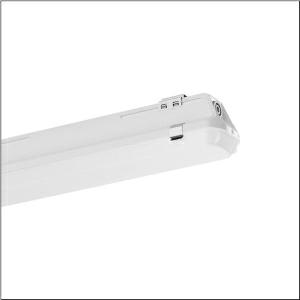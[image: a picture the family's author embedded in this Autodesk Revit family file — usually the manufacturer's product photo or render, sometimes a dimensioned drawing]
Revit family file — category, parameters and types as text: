
# Revit family: monsun_r__11_51fp10ep430h_21f7
name_source: partatom
category: Lighting Fixtures
units: mm (PartAtom-declared; Revit-internal decimal feet)

## family parameters
Cut with Voids When Loaded = No
Host = Face
Light Source = No
Part Type = Normal
Room Calculation Point = No
Round Connector Dimension = Use Diameter
Shared = No

## types (1)
- --- (1 x LED, 3840 lm, 22.3 W, 4000K)
    Apparent Load = 22 VA
    CIE Flux Codes = 47 77 93 94 100
    Color Rendering = 80
    Color Temperature = 4000K
    Default Elevation = 1800 mm
    Description = Monsun® 11, damp-proof luminaire, chain hanger, primary optical cover: enclosure, of PMMA, light emission: direct distribution, primary light characteristic: symmetric, installation type: suspended mounting, surface-mounted, horizontal mounting, vertical mounting, LED, rated luminous flux: 3.840lm, luminous efficacy: 172lm/W, light colour: 840, colour temperature: 4000K, control gear: ECG DALI, with terminal, 5-pole, max. 2.5mm², mains connection: 220..240V, AC, 50/60Hz, rated input power: 22W, luminaire housing, of glass-fibre reinforced polyester, uncoated, bright grey, incl. chain hanger, length: 1.590mm, width: 90mm, height: 88mm, clip for enclosure, of stainless steel (V2A), ceiling mounting element, of stainless steel (V2A), chain hanger, of stainless steel (V2A), protection rating (complete): IP66, insulation class (complete): insulation class I (protective earthing), certification: CE, ENEC, VDE, UKCA, protection symbol: D, impact resistance: IK04, permissible operating ambient temperature: -25..+40°C, standard: EN 50419, EN 60598-2-1, no direct snow, no direct sun, no direct rain, for indoor or canopied outdoor use, corresponds to IFS (International Featured Standards) requirements for safety and quality in the food industry, contact your sales advisor before using the luminaires in applications with unclear chemical exposure, large temperature fluctuations or condensation-forming humidity, LABS conformity tested according to VDMA 24364:2018-05, packaging unit: 1 piece
    Height = 89 mm
    Lamp = 1 x LED
    Lamp Light Flux = 3840 lm
    Lamp Power = 22.3 W
    Lamp count = 1
    Length = 1590 mm
    Luminous efficacy = 172 lm/W
    Manufacturer = Siteco
    ModVariant = No
    Model = 51FP10EP430H
    Mounting Place = Ceiling
    Mounting Type = Surface mounted
    Number of Poles = 1
    OnlyDefault = Yes
    Power Factor = 1
    Product Name = Monsun® 11
    Product group = damp-proof luminaire
    ProductGroupID = 300
    Protection Class = Protection class I
    Protection Degree = IP 66
    RLX_Detail_Level = 1
    RLX_Emergency_Light_Flux = 0 lm
    RLX_Emergency_Type = 0
    RLX_Emergency_Type_DB = No
    RlxData = <blob elided: 92289 chars, md5=1698bf2a>
    Socket = socket
    Standby Power = 0 W
    System Light Flux = 3840 lm
    System Power = 22 W
    Type Comments = factory setting: luminous flux: 100 % | dim-lin: 254 | 145 mA
    Type Image = l_1319650.jpg
    URL = http://relux.com
    VarID = @adj_174815
    Voltage = 0 V
    Weight = 0.00 kg
    Width = 90 mm

## geometry (parser evidence)
native form markers: Blend x4, Sweep x12
no freeform markers — native parametric forms only
